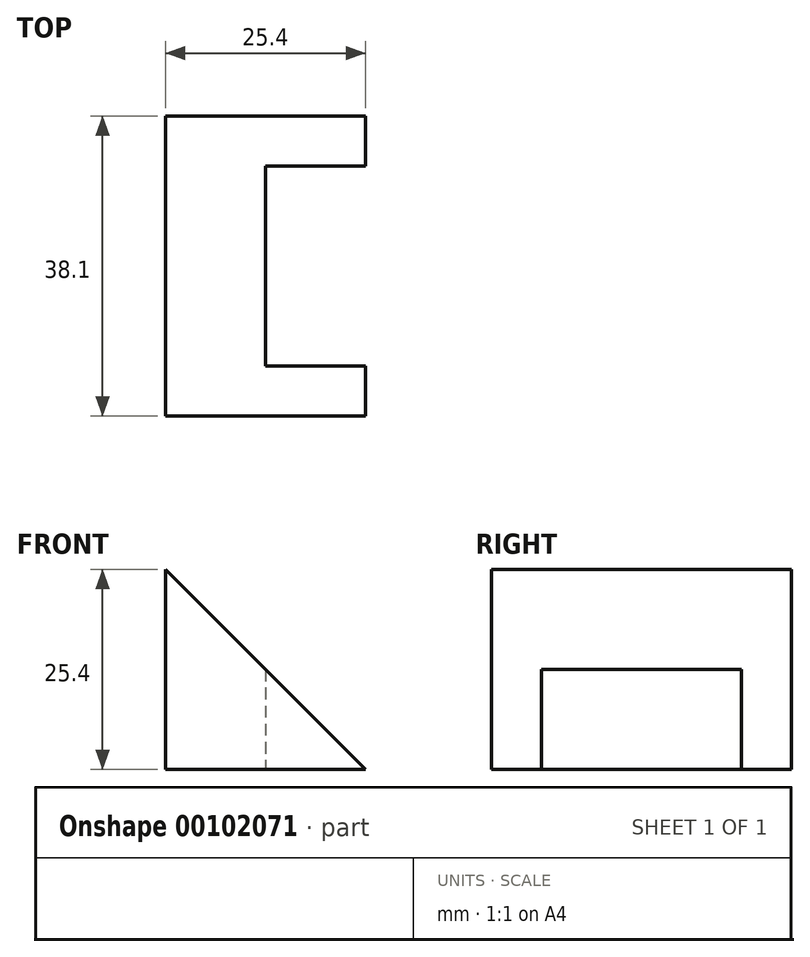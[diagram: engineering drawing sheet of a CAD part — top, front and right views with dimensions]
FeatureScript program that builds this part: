
annotation { "Feature Type Name" : "Feature", "Feature Type Description" : "" }
export const myFeature = defineFeature(function(context is Context, id is Id, definition is map)
    precondition{}
    {
        {
            var Q0;
            Q0=qCreatedBy(makeId("Front.planeOp"),FACE);
            var sketch = newSketch(context, id + "F0", { "sketchPlane" : qUnion([Q0])});
            skLineSegment(sketch, "E0", {"start": v(0, 0) * mm, "end": v(0, 25.4) * mm});
            skLineSegment(sketch, "E1", {"start": v(0, 25.4) * mm, "end": v(25.4, 0) * mm});
            skLineSegment(sketch, "E2", {"start": v(25.4, 0) * mm, "end": v(0, 0) * mm});
            skSolve(sketch);
        }
        {
            var Q0;
            Q0 = qSketchRegion(id + "F0", true);
            extrude(context, id + "F1", {"entities" : qUnion([Q0]), "endBound" : BoundingType.SYMMETRIC, "depth" : 38.1 * mm});
        }
        {
            var Q0;
            Q0=qCreatedBy(makeId("Top.planeOp"),FACE);
            var sketch = newSketch(context, id + "F2", { "sketchPlane" : qUnion([Q0])});
            skLineSegment(sketch, "E3.bottom", {"start": v(25.4, 12.7) * mm, "end": v(12.7, 12.7) * mm});
            skLineSegment(sketch, "E3.top", {"start": v(25.4, -12.7) * mm, "end": v(12.7, -12.7) * mm});
            skLineSegment(sketch, "E3.left", {"start": v(25.4, 12.7) * mm, "end": v(25.4, -12.7) * mm});
            skLineSegment(sketch, "E3.right", {"start": v(12.7, 12.7) * mm, "end": v(12.7, -12.7) * mm});
            skSolve(sketch);
        }
        {
            var Q0;
            Q0 = qSketchRegion(id + "F2", true);
            extrude(context, id + "F3", {"entities" : qUnion([Q0]), "operationType" : NewBodyOperationType.REMOVE, "depth" : 25.4 * mm});
        }
    });
